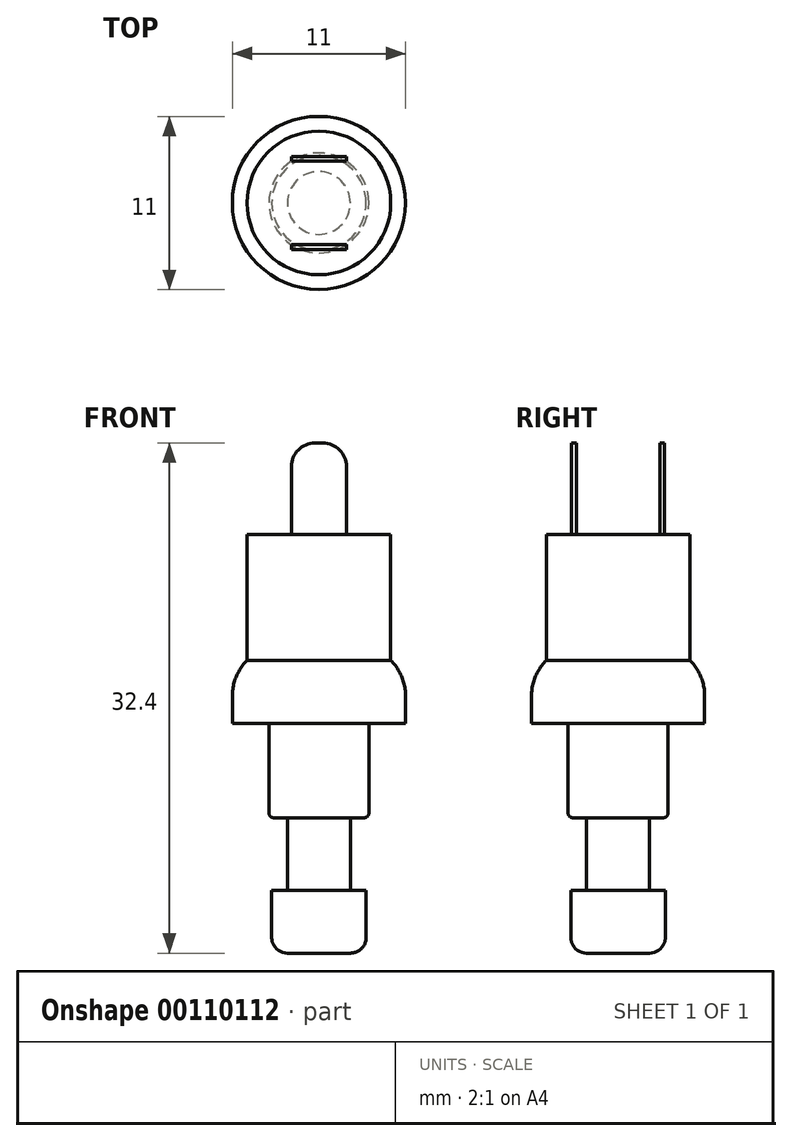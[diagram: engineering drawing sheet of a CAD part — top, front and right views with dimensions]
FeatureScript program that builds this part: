
annotation { "Feature Type Name" : "Feature", "Feature Type Description" : "" }
export const myFeature = defineFeature(function(context is Context, id is Id, definition is map)
    precondition{}
    {
        {
            var Q0;
            Q0=qCreatedBy(makeId("Top.planeOp"),FACE);
            var sketch = newSketch(context, id + "F0", { "sketchPlane" : qUnion([Q0])});
            skCircle(sketch, "E0", {"center": v(0, 0) * mm, "radius": 3 * mm});
            skSolve(sketch);
        }
        {
            var Q0;
            Q0=qSketchRegion(id+"F0",true);
            extrude(context, id + "F1", {"entities" : qUnion([Q0]), "depth" : 4 * mm});
        }
        {
            var Q0;
            Q0=makeQuery(id+"F1.opExtrude","CAP_FACE",FACE,{"disambiguationData":[OSD([sQuery(id+"F0.wireOp",EDGE,"E0")])],"isStart":false});
            var sketch = newSketch(context, id + "F2", { "sketchPlane" : qUnion([Q0])});
            skCircle(sketch, "E1", {"center": v(0, 0) * mm, "radius": 2 * mm});
            skSolve(sketch);
        }
        {
            var Q0;
            Q0=qSketchRegion(id+"F2",true);
            extrude(context, id + "F3", {"entities" : qUnion([Q0]), "operationType" : NewBodyOperationType.ADD, "depth" : 4.6 * mm});
        }
        {
            var Q0;
            Q0=makeQuery(id+"F3.opExtrude","CAP_FACE",FACE,{"disambiguationData":[OSD([sQuery(id+"F2.wireOp",EDGE,"E1")])],"isStart":false});
            var sketch = newSketch(context, id + "F4", { "sketchPlane" : qUnion([Q0])});
            skCircle(sketch, "E2", {"center": v(0, 0) * mm, "radius": 3.17 * mm});
            skSolve(sketch);
        }
        {
            var Q0;
            Q0=qSketchRegion(id+"F4",true);
            extrude(context, id + "F5", {"entities" : qUnion([Q0]), "operationType" : NewBodyOperationType.ADD, "depth" : 6 * mm});
        }
        {
            var Q0;
            Q0=makeQuery(id+"F5.opExtrude","CAP_FACE",FACE,{"disambiguationData":[OSD([sQuery(id+"F4.wireOp",EDGE,"E2")])],"isStart":false});
            var sketch = newSketch(context, id + "F6", { "sketchPlane" : qUnion([Q0])});
            skCircle(sketch, "E3", {"center": v(0, 0) * mm, "radius": 5.5 * mm});
            skSolve(sketch);
        }
        {
            var Q0;
            Q0=qSketchRegion(id+"F6",true);
            extrude(context, id + "F7", {"entities" : qUnion([Q0]), "operationType" : NewBodyOperationType.ADD, "depth" : 4 * mm});
        }
        {
            var Q0;
            Q0=makeQuery(id+"F7.opExtrude","CAP_FACE",FACE,{"disambiguationData":[OSD([sQuery(id+"F6.wireOp",EDGE,"E3")])],"isStart":false});
            var sketch = newSketch(context, id + "F8", { "sketchPlane" : qUnion([Q0])});
            skCircle(sketch, "E4", {"center": v(0, 0) * mm, "radius": 4.56 * mm});
            skSolve(sketch);
        }
        {
            var Q0;
            Q0=makeQuery(id+"F8.imprint","IMPRINT",FACE,{"disambiguationData":[TD([[makeQuery(id+"F8.imprint","IMPRINT",EDGE,{"derivedFrom":sQuery(id+"F8.wireOp",EDGE,"E4")}),1.0]])]});
            extrude(context, id + "F9", {"entities" : qUnion([Q0]), "operationType" : NewBodyOperationType.ADD, "depth" : 8 * mm});
        }
        {
            var Q0;
            Q0=makeQuery(id+"F7.opExtrude","CAP_EDGE",EDGE,{"disambiguationData":[OSD([sQuery(id+"F6.wireOp",EDGE,"E3")])],"isStart":false});
            fillet(context, id + "F10", {"entities" : qUnion([Q0]), "radius" : 3.2 * mm, "tangentPropagation" : true, "allowEdgeOverflow" : false});
        }
        {
            var Q0;
            Q0=makeQuery(id+"F1.opExtrude","CAP_EDGE",EDGE,{"disambiguationData":[OSD([sQuery(id+"F0.wireOp",EDGE,"E0")])],"isStart":true});
            fillet(context, id + "F11", {"entities" : qUnion([Q0]), "radius" : 1 * mm, "tangentPropagation" : true, "allowEdgeOverflow" : false});
        }
        {
            var Q0;
            Q0=makeQuery(id+"F5.opExtrude","CAP_EDGE",EDGE,{"disambiguationData":[OSD([sQuery(id+"F4.wireOp",EDGE,"E2")])],"isStart":true});
            fillet(context, id + "F12", {"entities" : qUnion([Q0]), "radius" : .3 * mm, "tangentPropagation" : true, "allowEdgeOverflow" : false});
        }
        {
            var Q0;
            Q0=makeQuery(id+"F9.opExtrude","CAP_FACE",FACE,{"disambiguationData":[OSD([sQuery(id+"F8.wireOp",EDGE,"E4")])],"isStart":false});
            var sketch = newSketch(context, id + "F13", { "sketchPlane" : qUnion([Q0])});
            skLineSegment(sketch, "E5.rect.bottom", {"start": v(1.75, 2.96) * mm, "end": v(-1.75, 2.96) * mm});
            skLineSegment(sketch, "E5.rect.top", {"start": v(1.75, -2.96) * mm, "end": v(-1.75, -2.96) * mm});
            skLineSegment(sketch, "E5.rect.left", {"start": v(1.75, 2.96) * mm, "end": v(1.75, 2.66) * mm});
            skLineSegment(sketch, "E5.rect.right", {"start": v(-1.75, 2.96) * mm, "end": v(-1.75, 2.66) * mm});
            skPoint(sketch, "E5.rect.middle", {"position": v(0, 0) * mm});
            skLineSegment(sketch, "E6", {"start": v(-1.75, -2.66) * mm, "end": v(1.75, -2.66) * mm});
            skLineSegment(sketch, "E7", {"start": v(-1.75, 2.66) * mm, "end": v(1.75, 2.66) * mm});
            skLineSegment(sketch, "E8.trimOffspring", {"start": v(-1.75, -2.66) * mm, "end": v(-1.75, -2.96) * mm});
            skLineSegment(sketch, "E9.trimOffspring", {"start": v(1.75, -2.66) * mm, "end": v(1.75, -2.96) * mm});
            skSolve(sketch);
        }
        {
            var Q0;
            Q0=qSketchRegion(id+"F13",true);
            extrude(context, id + "F14", {"entities" : qUnion([Q0]), "operationType" : NewBodyOperationType.ADD, "depth" : 5.8 * mm});
        }
        {
            var Q0;
            Q0=makeQuery(id+"F14.opExtrude","CAP_EDGE",EDGE,{"disambiguationData":[OSD([sQuery(id+"F13.wireOp",EDGE,"E5.rect.left")])],"isStart":false});
            var Q1;
            Q1=makeQuery(id+"F14.opExtrude","CAP_EDGE",EDGE,{"disambiguationData":[OSD([sQuery(id+"F13.wireOp",EDGE,"E9.trimOffspring")])],"isStart":false});
            var Q2;
            Q2=makeQuery(id+"F14.opExtrude","CAP_EDGE",EDGE,{"disambiguationData":[OSD([sQuery(id+"F13.wireOp",EDGE,"E8.trimOffspring")])],"isStart":false});
            var Q3;
            Q3=makeQuery(id+"F14.opExtrude","CAP_EDGE",EDGE,{"disambiguationData":[OSD([sQuery(id+"F13.wireOp",EDGE,"E5.rect.right")])],"isStart":false});
            fillet(context, id + "F15", {"entities" : qUnion([Q0, Q1, Q2, Q3]), "radius" : 1.5 * mm, "tangentPropagation" : true, "allowEdgeOverflow" : false});
        }
    });
